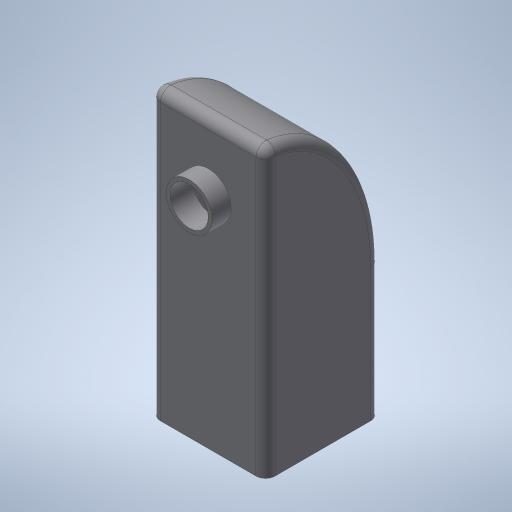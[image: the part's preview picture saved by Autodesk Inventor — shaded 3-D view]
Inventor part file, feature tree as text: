
AUTODESK INVENTOR PART (.ipt)
format: ipt  version: 2023.1 (Build 271208000, 208)  size: 356,352 bytes
history: native  units: mm
features: extrude x6, sketch x6, projected_geometry x3, fillet x2, shell x1
ambient origin geometry x8: Origin, YZ Plane, XZ Plane, XY Plane, X Axis, Y Axis, Z Axis, Center Point
bodies: Solid1 (feature_tree)
feature tree (18):
  extrude  "Extrusion1"  Depth=60.0mm
  extrude  "Extrusion2"  Depth=80.0mm
  shell  "Shell1"  Thickness=60.0mm
  extrude  "Extrusion3"  Depth=30.0mm
  extrude  "Extrusion4"  Depth=20.0mm
  extrude  "Extrusion5"  Depth=5.0mm
  extrude  "Extrusion6"  Depth=5.0mm
  fillet  "Fillet1"  Radius=20.0mm
  fillet  "Fillet2"  Radius=60.0mm
  sketch  "Sketch1"  dims[d0=60.0mm d1=60.0mm]
  sketch  "Sketch2"  dims[d2=70.0mm d3=0.0mm d4=80.0mm d5=60.0mm d6=0.0mm]
  sketch  "Sketch3"  dims[d7=2.0mm d8=30.0mm]
  sketch  "Sketch4"  dims[d9=35.0mm d10=20.0mm]
  projected_geometry  "Projected Loop1"
  sketch  "Sketch5"  dims[d11=5.0mm d12=0.0mm d13=2.0mm]
  projected_geometry  "Projected Loop2"
  sketch  "Sketch6"  dims[d14=10.0mm d15=0.0mm d16=35.0mm d17=20.0mm d18=60.0mm d19=10.0mm d20=0.0mm d21=2.0mm d22=1.0mm d23=0.0mm d24=5.0mm d25=5.0mm]
  projected_geometry  "Projected Loop3"
